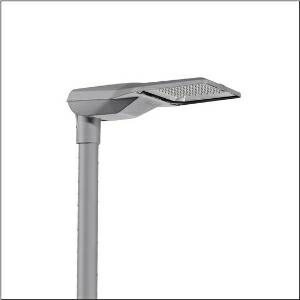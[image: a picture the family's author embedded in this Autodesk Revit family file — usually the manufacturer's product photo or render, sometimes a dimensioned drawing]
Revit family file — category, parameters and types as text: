
# Revit family: streetlight_sl_21_iq_midi___st1_5a_5xe3p41d08mb_62ad
name_source: partatom
category: Lighting Fixtures
units: mm (PartAtom-declared; Revit-internal decimal feet)

## family parameters
Cut with Voids When Loaded = No
Host = Face
Light Source = No
Part Type = Normal
Room Calculation Point = No
Round Connector Dimension = Use Diameter
Shared = No

## types (1)
- --- (1 x LED, 20000 lm, 146.7 W, 4000K)
    Apparent Load = 147 VA
    CIE Flux Codes = 22 53 95 100 100
    Color Rendering = 70
    Color Temperature = 4000K
    Default Elevation = 1800 mm
    Description = Streetlight SL 21 iQ midi, mast luminaire, primary light control with lens, of PMMA, primary optical cover: cover, of toughened safety glass, transparent, light distribution: ST1.5a, light emission: direct distribution, primary light characteristic: asymmetric, installation type: post-top, side-entry, LED, High Power LED, rated luminous flux: 20.000lm, luminous efficacy: 136lm/W, light colour: 740, colour temperature: 4000K, control gear: iQ-Comfort, control: Auto-Match, Temp-Guard, Lumen-Switch, Night-Set, Smart-Wire, Light-Fading, Desk-Remote (wireless, voltage-free reading and setting of iQ features in the workshop via application-optimized NFC function/RFID function), optimised constant luminous flux control (CLO 2.0), pre-setting: linear dimming characteristic, mains connection: 230..240V, AC, 50/60Hz, start of lifetime: 147W, end of service life: 161W, reduction: 62W, luminaire housing, of diecast aluminium, powder-coated, SITECO metallic grey (DB 702S), corrosivity category C5 high according to DIN EN ISO 12944, please order mast flange separately, inclination adjustable: 0°, 5°, 10°, 15°, sealing non-destructively replaceable, multi-level sealing system, length: 644mm, width: 335mm, height: 110mm, mast flange for spigot size: 42mm (side-entry): 5XC10008XM4, 60/48mm (side-entry/post-top): 5XC10108XM2, 76/60mm (side-entry/post-top): 5XC10108XM1, mounting height: 4..8m, protection rating (complete): IP66, insulation class (complete): insulation class II (safety insulation), certification: CE, ENEC, ENEC+, VDE, impact resistance: IK10, permissible operating ambient temperature for outdoor applications: -40..+50°C, standard-compliant lighting for roads and squares, packaging unit: 1 piece

Light Distribution: ST1.5a
    Height = 111 mm
    Lamp = 1 x LED
    Lamp Light Flux = 20000 lm
    Lamp Power = 146.7 W
    Lamp count = 1
    Length = 644 mm
    Luminous efficacy = 136 lm/W
    Manufacturer = Siteco
    ModVariant = No
    Model = 5XE3P41D08MB
    Number of Poles = 1
    OnlyDefault = Yes
    Power Factor = 1
    Product Name = Streetlight SL 21 iQ midi | ST1.5a
    Product group = mast luminaire | pylon top
    ProductGroupID = 6100
    Protection Class = Protection class II
    Protection Degree = IP 66
    RLX_Detail_Level = 1
    RLX_Emergency_Light_Flux = 0 lm
    RLX_Emergency_Type = 0
    RLX_Emergency_Type_DB = No
    RlxData = <blob elided: 30477 chars, md5=0e407a66>
    Socket = socket
    Standby Power = 0 W
    System Light Flux = 20000 lm
    System Power = 147 W
    Type Comments = factory setting: luminous flux: 100 % | dim-lin: 254 | 753 mA
    Type Image = l_1004298.jpg
    URL = http://relux.com
    VarID = @adj_175735
    Voltage = 0 V
    Weight = 0.00 kg
    Width = 336 mm

## geometry (parser evidence)
native form markers: Blend x4, Sweep x8
no freeform markers — native parametric forms only
